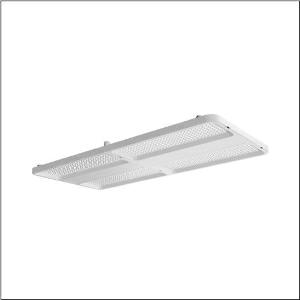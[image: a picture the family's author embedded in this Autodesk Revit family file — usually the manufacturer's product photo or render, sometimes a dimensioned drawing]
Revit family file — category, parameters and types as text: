
# Revit family: highbay_21_maxi_52hn11db4mda
name_source: partatom
category: Lighting Fixtures
units: mm (PartAtom-declared; Revit-internal decimal feet)

## family parameters
Cut with Voids When Loaded = No
Host = Face
Light Source = No
Part Type = Normal
Room Calculation Point = No
Round Connector Dimension = Use Diameter
Shared = No

## types (1)
- --- (1 x LED, 4230 lm, 22.6 W, 4000K)
    Apparent Load = 23 VA
    CIE Flux Codes = 89 97 99 100 100
    Color Rendering = 80
    Color Temperature = 4000K
    Default Elevation = 1800 mm
    Description = high bay luminaire Highbay 21 maxi; direct symmetric narrow distribution, light control with lens of PMMA; UGR ≤ 19 (X = 4H | Y = 8H | S = 0.25H | reflection values 70/50/20); luminous flux: 28.000lm; light colour: 840, colour temperature: 4000K, MacAdam ≤ 3 SDCM (initial), colour rendering: CRI > 80; luminous efficacy: 194,4lm/W; rated service life: 75.000h (L80) at AT= ta max; control: DALI 2; luminaire connection: terminal, 5-pole, max. 2.5mm² (cable entry for one cable, Ø 8.5..16mm); mains connection: 230..240V, AC/DC 0/50..60Hz; connected load: 144W; protection rating (complete): IP66; insulation class (complete): insulation class I (protective earthing); protection symbol: D; impact resistance: IK08; certification: CE, ENEC, VDE, UKCA; luminaire for central battery installations according to EN 60598-2-22, internal wiring halogen-free; luminaire LABS conformity tested according to VDMA 24364:2018-05; Suitable for use in the food industry according to the specifications of IFS-Food, HACCP and/or BRC; housing frame of high-performance plastic PA6, matt traffic white (RAL 9016); cover of PMMA; dimension (LxWxH): 946 x 442 x 72mm; permissible operating ambient temperature: -40..+65°C (reducing of maximum allowable ambient temperature of 5°C with ceiling mounting); packaging unit: 1 piece; (delivery without accessories; please order mounting accessories separately)
    Height = 72 mm  [stored 0.23622 ft]
    Lamp = 1 x LED
    Lamp Light Flux = 4230 lm
    Lamp Power = 22.6 W
    Lamp count = 1
    Length = 946 mm
    Luminous efficacy = 187 lm/W
    Manufacturer = Siteco
    ModVariant = No
    Model = 52HN11DB4MDA
    Mounting Place = Ceiling
    Mounting Type = Pendant
    Number of Poles = 1
    OnlyDefault = Yes
    Power Factor = 1
    Product Name = Highbay 21 maxi
    Product group = high bay luminaire
    ProductGroupID = 902
    Protection Class = Protection class I
    Protection Degree = IP 66
    RLX_Detail_Level = 1
    RLX_Emergency_Light_Flux = 0 lm
    RLX_Emergency_Type = 0
    RLX_Emergency_Type_DB = No
    RlxData = <blob elided: 128225 chars, md5=9f0c6201>
    Socket = socket
    Standby Power = 0 W
    System Light Flux = 4230 lm
    System Power = 23 W
    Type Comments = : DC mode (central or group accumulator) initial emergency light level
    Type Image = l_1363244.jpg
    URL = http://relux.com
    VarID = @adj_017777
    Voltage = 0 V
    Weight = 0.00 kg
    Width = 442 mm

note: [stored X ft] marks values corroborated as IEEE doubles in the binary element streams (Revit-internal decimal feet)

## geometry (parser evidence)
native form markers: Blend x4, Sweep x10
no freeform markers — native parametric forms only
